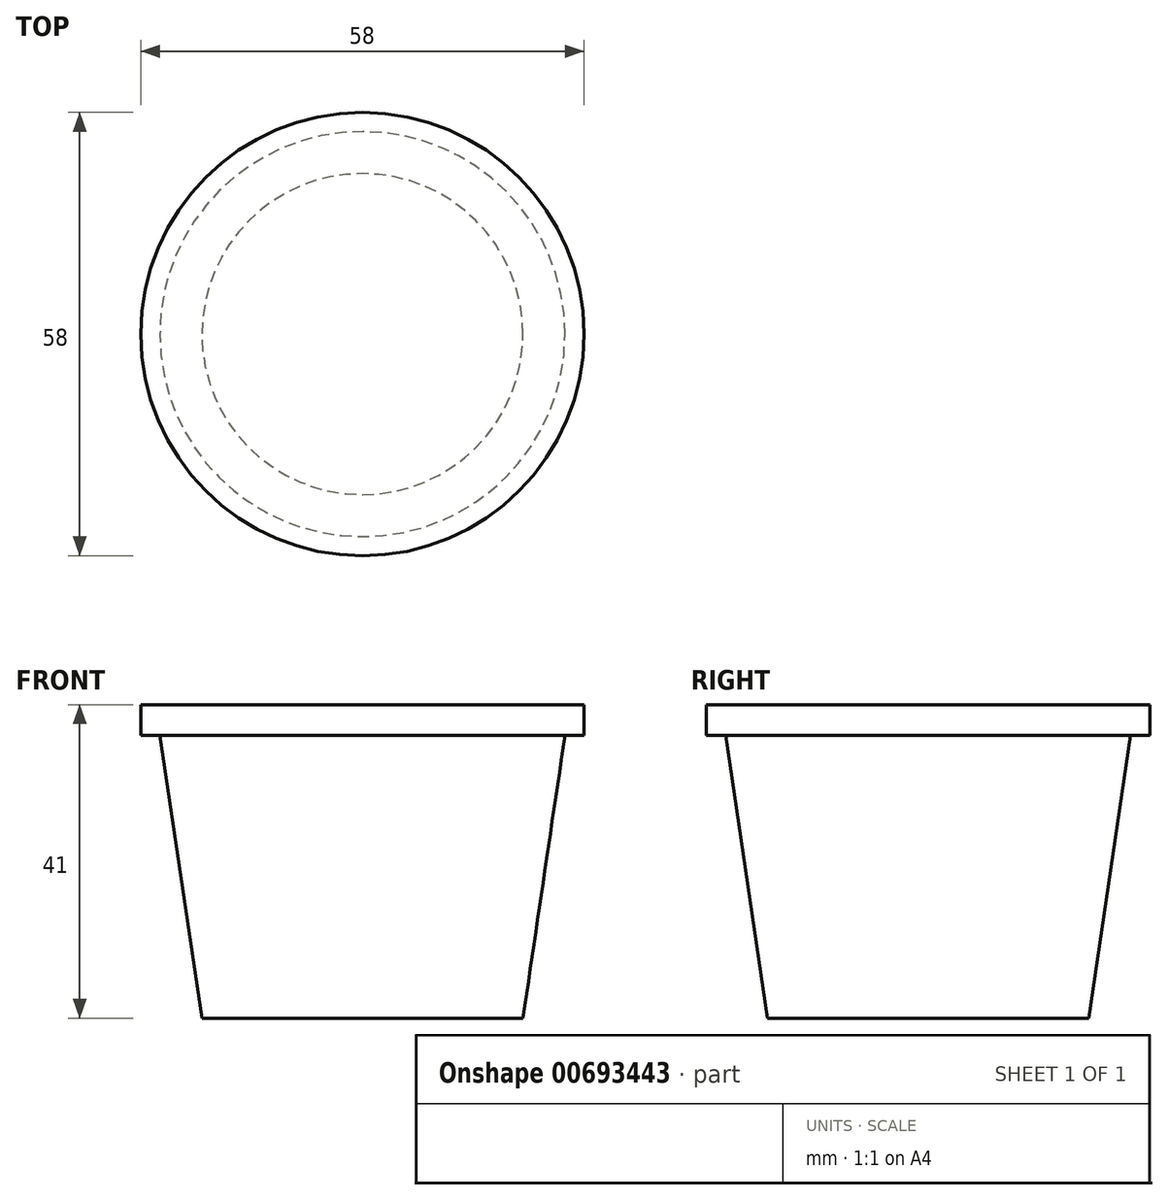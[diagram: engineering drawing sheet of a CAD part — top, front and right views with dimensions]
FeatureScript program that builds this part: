
annotation { "Feature Type Name" : "Feature", "Feature Type Description" : "" }
export const myFeature = defineFeature(function(context is Context, id is Id, definition is map)
    precondition{}
    {
        {
            var Q0;
            Q0=qCreatedBy(makeId("Top.planeOp"),FACE);
            var sketch = newSketch(context, id + "F0", { "sketchPlane" : qUnion([Q0])});
            skCircle(sketch, "E0", {"center": v(0, 0) * mm, "radius": 21 * mm});
            skSolve(sketch);
        }
        {
            var Q0;
            Q0=qCreatedBy(makeId("Top.planeOp"),FACE);
            cPlane(context, id + "F1", {"entities" : qUnion([Q0]), "cplaneType" : CPlaneType.OFFSET, "offset" : 37 * mm, "width" : 150 * mm, "height" : 150 * mm});
        }
        {
            var Q0;
            Q0=qCreatedBy(makeId("Top.planeOp"),FACE);
            cPlane(context, id + "F2", {"entities" : qUnion([Q0]), "cplaneType" : CPlaneType.OFFSET, "offset" : 41 * mm, "width" : 150 * mm, "height" : 150 * mm});
        }
        {
            var Q0;
            Q0=qCreatedBy(id+"F1.planeOp",FACE);
            var sketch = newSketch(context, id + "F3", { "sketchPlane" : qUnion([Q0])});
            skCircle(sketch, "E1", {"center": v(0, 0) * mm, "radius": 26.5 * mm});
            skSolve(sketch);
        }
        {
            var Q0;
            Q0=makeQuery(id+"F0.imprint","IMPRINT",FACE,{"disambiguationData":[TD([[makeQuery(id+"F0.imprint","IMPRINT",EDGE,{"derivedFrom":sQuery(id+"F0.wireOp",EDGE,"E0")}),1.0]])]});
            var Q1;
            Q1=makeQuery(id+"F3.imprint","IMPRINT",FACE,{"disambiguationData":[TD([[makeQuery(id+"F3.imprint","IMPRINT",EDGE,{"derivedFrom":sQuery(id+"F3.wireOp",EDGE,"E1")}),1.0]])]});
            loft(context, id + "F4", {"sheetProfilesArray" : [{ "sheetProfileEntities" : qUnion([Q0]) }, { "sheetProfileEntities" : qUnion([Q1]) }]});
        }
        {
            var Q0;
            Q0=qCreatedBy(id+"F2.planeOp",FACE);
            var sketch = newSketch(context, id + "F5", { "sketchPlane" : qUnion([Q0])});
            skCircle(sketch, "E2", {"center": v(0, 0) * mm, "radius": 29 * mm});
            skSolve(sketch);
        }
        {
            var Q0;
            Q0=qCreatedBy(id+"F1.planeOp",FACE);
            var sketch = newSketch(context, id + "F6", { "sketchPlane" : qUnion([Q0])});
            skCircle(sketch, "E3", {"center": v(0, 0) * mm, "radius": 29 * mm});
            skSolve(sketch);
        }
        {
            var Q1;
            Q1=makeQuery(id+"F6.imprint","IMPRINT",FACE,{"disambiguationData":[TD([[makeQuery(id+"F6.imprint","IMPRINT",EDGE,{"derivedFrom":sQuery(id+"F6.wireOp",EDGE,"E3")}),1.0]])]});
            var Q2;
            Q2=makeQuery(id+"F5.imprint","IMPRINT",FACE,{"disambiguationData":[TD([[makeQuery(id+"F5.imprint","IMPRINT",EDGE,{"derivedFrom":sQuery(id+"F5.wireOp",EDGE,"E2")}),1.0]])]});
            loft(context, id + "F7", {"operationType" : NewBodyOperationType.ADD, "sheetProfilesArray" : [{ "sheetProfileEntities" : qUnion([Q1]) }, { "sheetProfileEntities" : qUnion([Q2]) }]});
        }
    });
